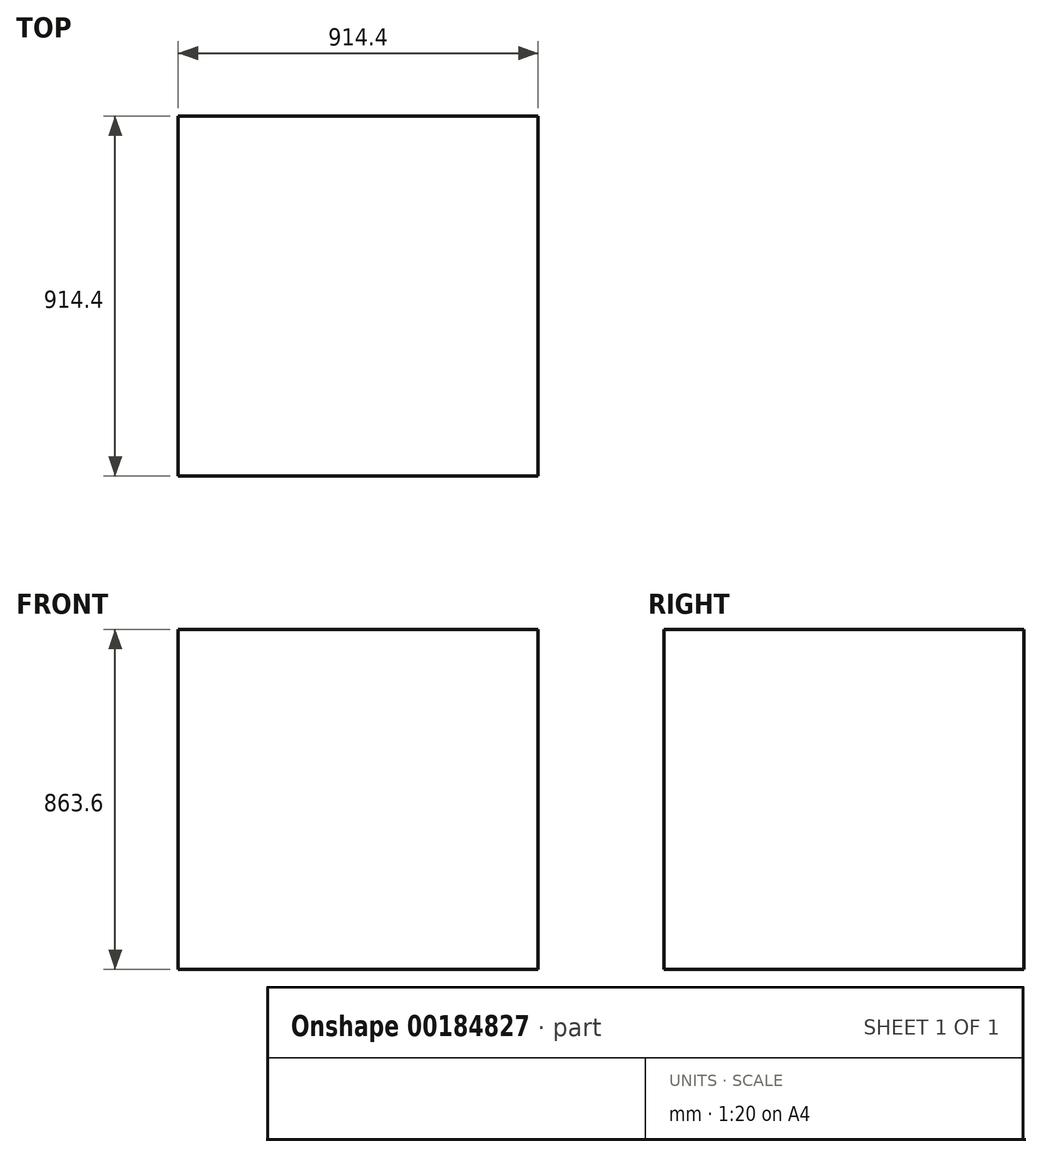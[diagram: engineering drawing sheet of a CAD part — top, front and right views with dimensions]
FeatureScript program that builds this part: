
annotation { "Feature Type Name" : "Feature", "Feature Type Description" : "" }
export const myFeature = defineFeature(function(context is Context, id is Id, definition is map)
    precondition{}
    {
        {
            var Q0;
            Q0=qCreatedBy(makeId("Top.planeOp"),FACE);
            var sketch = newSketch(context, id + "F0", { "sketchPlane" : qUnion([Q0])});
            skLineSegment(sketch, "E0.bottom", {"start": v(457.2, -457.2) * mm, "end": v(-457.2, -457.2) * mm});
            skLineSegment(sketch, "E0.top", {"start": v(457.2, 457.2) * mm, "end": v(-457.2, 457.2) * mm});
            skLineSegment(sketch, "E0.left", {"start": v(457.2, -457.2) * mm, "end": v(457.2, 457.2) * mm});
            skLineSegment(sketch, "E0.right", {"start": v(-457.2, -457.2) * mm, "end": v(-457.2, 457.2) * mm});
            skPoint(sketch, "E0.middle", {"position": v(0, 0) * mm});
            skSolve(sketch);
        }
        {
            var Q0;
            Q0=makeQuery(id+"F0.imprint","IMPRINT",FACE,{"disambiguationData":[TD([[makeQuery(id+"F0.imprint","IMPRINT",EDGE,{"derivedFrom":sQuery(id+"F0.wireOp",EDGE,"E0.bottom")}),-1.0]])]});
            extrude(context, id + "F1", {"entities" : qUnion([Q0]), "depth" : 863.6 * mm});
        }
    });
